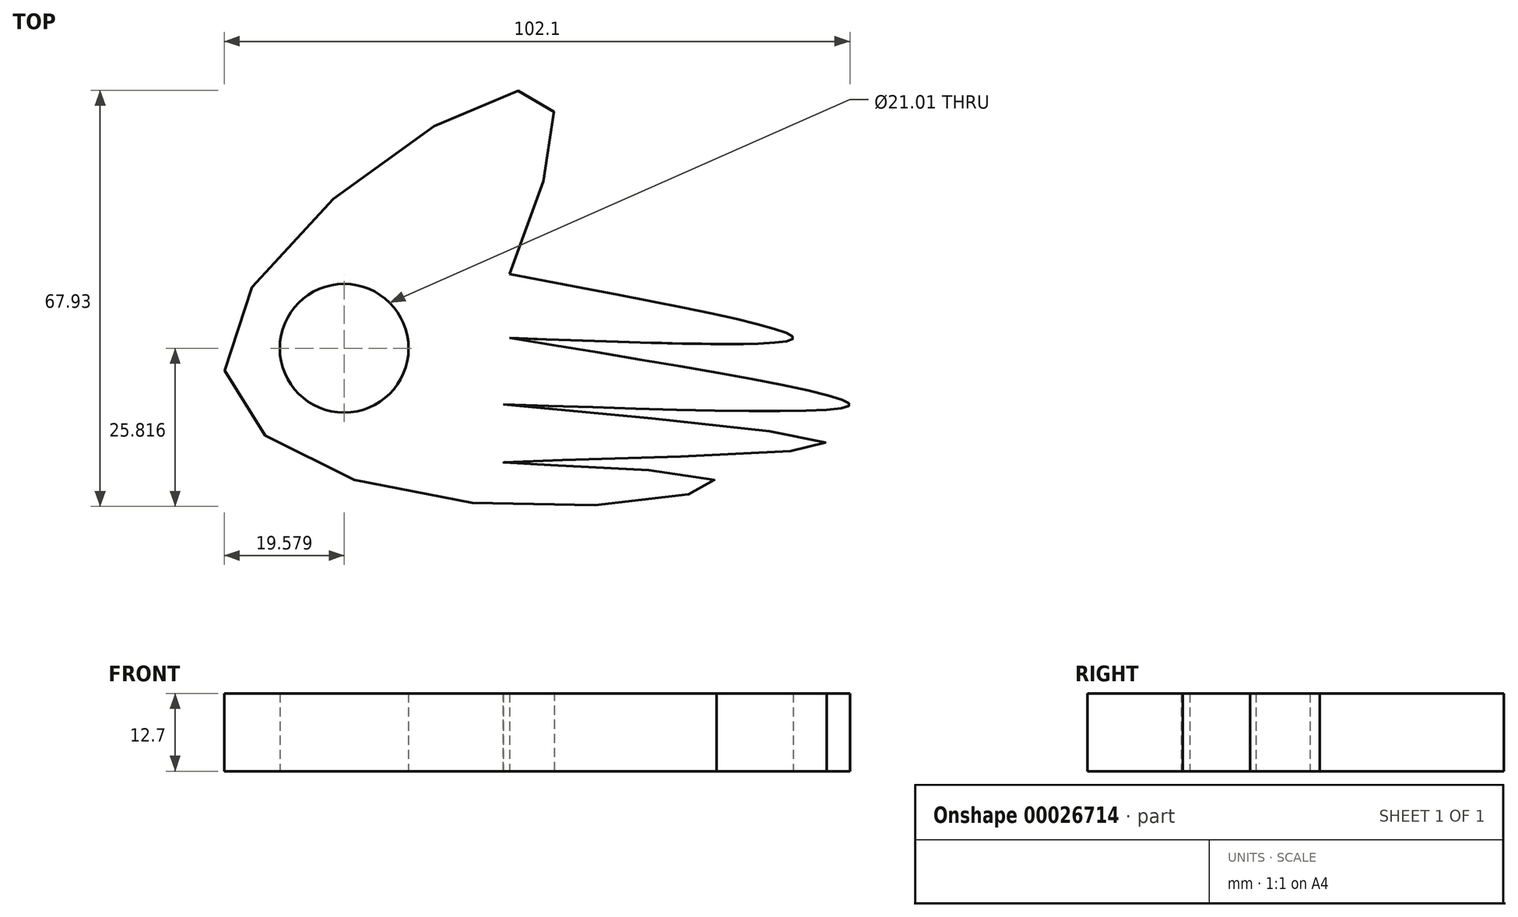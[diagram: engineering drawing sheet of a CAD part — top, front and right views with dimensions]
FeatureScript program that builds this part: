
annotation { "Feature Type Name" : "Feature", "Feature Type Description" : "" }
export const myFeature = defineFeature(function(context is Context, id is Id, definition is map)
    precondition{}
    {
        {
            var Q0;
            Q0=qCreatedBy(makeId("Top.planeOp"),FACE);
            var sketch = newSketch(context, id + "F0", { "sketchPlane" : qUnion([Q0])});
            skFitSpline(sketch, "E0", {"points": [v(16.79, 3.18) * mm, v(72.34, -7.72) * mm, v(15.82, -7.65) * mm], "startDerivative": vector(167.14, -27.28) * mm, "endDerivative": vector(-169.12, 5.61) * mm});
            skFitSpline(sketch, "E1", {"points": [v(16.79, 3.18) * mm, v(63.09, 3.18) * mm, v(16.79, 13.6) * mm], "startDerivative": vector(139.2, -5.14) * mm, "endDerivative": vector(-138.63, 25.9) * mm});
            skFitSpline(sketch, "E2", {"points": [v(15.82, -7.65) * mm, v(67.36, -14.68) * mm, v(15.82, -17.16) * mm, v(49.83, -19.8) * mm, v(12.47, -23.88) * mm, v(-29.42, 2.39) * mm, v(21.03, 43.5) * mm, v(16.79, 13.6) * mm], "startDerivative": vector(576.41, -53.1) * mm, "endDerivative": vector(-141.86, -365.48) * mm});
            skCircle(sketch, "E3", {"center": v(-10.18, 1.5) * mm, "radius": 10.5 * mm});
            skSolve(sketch);
        }
        {
            var Q0;
            Q0=makeQuery(id+"F0.imprint","IMPRINT",FACE,{"disambiguationData":[TD([[makeQuery(id+"F0.imprint","IMPRINT",EDGE,{"derivedFrom":sQuery(id+"F0.wireOp",EDGE,"E0")}),-1.0]])]});
            extrude(context, id + "F1", {"entities" : qUnion([Q0]), "depth" : 12.7 * mm});
        }
    });
